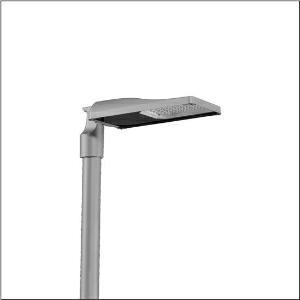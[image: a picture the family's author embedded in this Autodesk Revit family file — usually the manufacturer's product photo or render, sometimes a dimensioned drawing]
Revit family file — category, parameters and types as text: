
# Revit family: streetlight_sl_31_mini___st1_0a_5xh6d3ab08ha_9874
name_source: partatom
category: Lighting Fixtures
units: mm (PartAtom-declared; Revit-internal decimal feet)

## family parameters
Cut with Voids When Loaded = No
Host = Face
Light Source = No
Part Type = Normal
Room Calculation Point = No
Round Connector Dimension = Use Diameter
Shared = No

## types (1)
- --- (1 x LED, 9240 lm, 68.3 W, 3000K)
    Apparent Load = 68 VA
    CIE Flux Codes = 37 72 97 100 100
    Color Rendering = 70
    Color Temperature = 3000K
    Default Elevation = 1800 mm
    Description = Streetlight SL 31 mini, mast luminaire, primary light control with lens, of PMMA, primary optical cover: cover, of toughened safety glass, transparent, light distribution: ST1.0a, light emission: direct distribution, primary light characteristic: asymmetric, installation type: post-top, side-entry, LED, High Power LED, rated luminous flux: 9.240lm, luminous efficacy: 135lm/W, light colour: 730, colour temperature: 3000K, control: presetting dimming linear, flexible luminous flux parameterisation, time-dependent luminous flux control, constant luminous flux control, power reduction, intelligent temperature release in ECG and LED module, overheat protection, with cable H07RN-F 3x 1.5mm², mains connection: 220..240V, AC, 50/60Hz, connection cable pre-assembled, cable length: 8,5m, start of lifetime: 68W, end of service life: 75W, reduction: 30W, luminaire housing, of diecast aluminium, powder-coated, Siteco® metallic grey (DB 702S), corrosivity category C5 high according to DIN EN ISO 12944, no sealing on luminaire upper side, inclination: -15°..+20° (post-top) | -20°..+20° (side-entry), adjustable in 5° steps, mast flange (76/60mm) included as standard, multi-level sealing system, sealing non-destructively replaceable, protection rating (complete): IP66, insulation class (complete): insulation class II (safety insulation), certification: CE, ENEC, ENEC+, VDE, UKCA, impact resistance: IK09, permissible operating ambient temperature for outdoor applications: -40..+50°C, standard-compliant lighting for roads and squares, packaging unit: 1 piece

Light Distribution: ST1.0a
    Height = 76 mm
    Lamp = 1 x LED
    Lamp Light Flux = 9240 lm
    Lamp Power = 68.3 W
    Lamp count = 1
    Length = 547 mm
    Luminous efficacy = 135 lm/W
    Manufacturer = Siteco
    ModVariant = No
    Model = 5XH6D3AB08HA
    Number of Poles = 1
    OnlyDefault = Yes
    Power Factor = 1
    Product Name = Streetlight SL 31 mini | ST1.0a
    Product group = mast luminaire | pylon top
    ProductGroupID = 6100
    Protection Class = Protection class II
    Protection Degree = IP 66
    RLX_Detail_Level = 1
    RLX_Emergency_Light_Flux = 0 lm
    RLX_Emergency_Type = 0
    RLX_Emergency_Type_DB = No
    RlxData = <blob elided: 39741 chars, md5=f1edc5ef>
    Socket = socket
    Standby Power = 0 W
    System Light Flux = 9240 lm
    System Power = 68 W
    Type Comments = factory setting: luminous flux: 100 % | dim-lin: 254 | 693 mA
    Type Image = l_1300326.jpg
    URL = http://relux.com
    VarID = @adj_012105
    Voltage = 0 V
    Weight = 0.00 kg
    Width = 265 mm

## geometry (parser evidence)
native form markers: Blend x4, Sweep x10
no freeform markers — native parametric forms only
